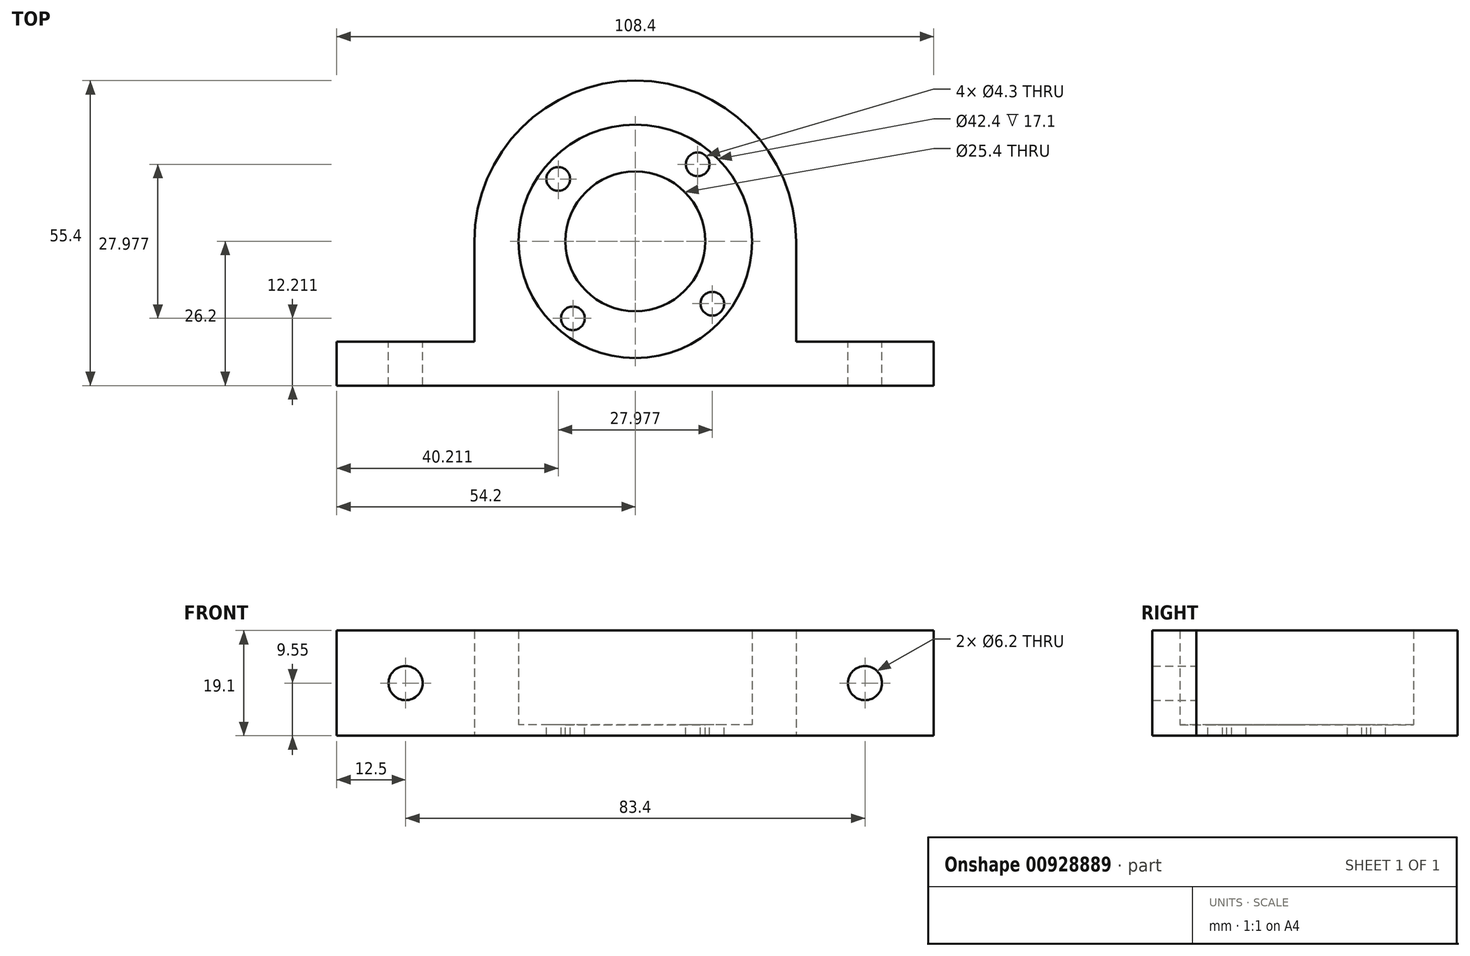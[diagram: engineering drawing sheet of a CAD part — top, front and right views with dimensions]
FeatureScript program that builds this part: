
annotation { "Feature Type Name" : "Feature", "Feature Type Description" : "" }
export const myFeature = defineFeature(function(context is Context, id is Id, definition is map)
    precondition{}
    {
        {
            var Q0;
            Q0=qCreatedBy(makeId("Top.planeOp"),FACE);
            var sketch = newSketch(context, id + "F0", { "sketchPlane" : qUnion([Q0])});
            skCircle(sketch, "E0", {"center": v(0, 0) * mm, "radius": 21.2 * mm});
            skCircle(sketch, "E1", {"center": v(0, 0) * mm, "radius": 26.2 * mm, "construction": true});
            skLineSegment(sketch, "E2", {"start": v(-64.12, -26.2) * mm, "end": v(71.3, -26.2) * mm, "construction": true});
            skLineSegment(sketch, "E3", {"start": v(54.2, -26.2) * mm, "end": v(-54.2, -26.2) * mm});
            skLineSegment(sketch, "E4", {"start": v(-54.2, -26.2) * mm, "end": v(-54.2, -18.2) * mm});
            skLineSegment(sketch, "E5", {"start": v(-54.2, -18.2) * mm, "end": v(-29.2, -18.2) * mm});
            skLineSegment(sketch, "E6", {"start": v(-29.2, -18.2) * mm, "end": v(-29.2, 0) * mm});
            skLineSegment(sketch, "E7", {"start": v(29.2, 0) * mm, "end": v(29.2, -18.2) * mm});
            skLineSegment(sketch, "E8", {"start": v(29.2, -18.2) * mm, "end": v(54.2, -18.2) * mm});
            skLineSegment(sketch, "E9", {"start": v(54.2, -18.2) * mm, "end": v(54.2, -26.2) * mm});
            skArc(sketch, "E10", {"start": v(29.2, 0) * mm, "mid": v(0, 29.2) * mm, "end": v(-29.2, 0) * mm});
            skSolve(sketch);
        }
        {
            var Q0;
            Q0=makeQuery(id+"F0.imprint","IMPRINT",FACE,{"disambiguationData":[TD([[makeQuery(id+"F0.imprint","IMPRINT",EDGE,{"derivedFrom":sQuery(id+"F0.wireOp",EDGE,"E0")}),-1.0]])]});
            extrude(context, id + "F1", {"entities" : qUnion([Q0]), "depth" : 17.1 * mm, "offsetDistance" : 25 * mm});
        }
        {
            var Q0;
            Q0=makeQuery(id+"F1.opExtrude","CAP_FACE",FACE,{"disambiguationData":[OSD([sQuery(id+"F0.wireOp",EDGE,"E0"),sQuery(id+"F0.wireOp",EDGE,"E3"),sQuery(id+"F0.wireOp",EDGE,"E4"),sQuery(id+"F0.wireOp",EDGE,"E5"),sQuery(id+"F0.wireOp",EDGE,"E6"),sQuery(id+"F0.wireOp",EDGE,"E7"),sQuery(id+"F0.wireOp",EDGE,"E8"),sQuery(id+"F0.wireOp",EDGE,"E9"),sQuery(id+"F0.wireOp",EDGE,"E10")])],"isStart":true});
            var sketch = newSketch(context, id + "F2", { "sketchPlane" : qUnion([Q0])});
            skCircle(sketch, "E11", {"center": v(0, 0) * mm, "radius": 12.7 * mm});
            skArc(sketch, "E12", {"start": v(-29.2, 0) * mm, "mid": v(0, -29.2) * mm, "end": v(29.2, 0) * mm});
            skLineSegment(sketch, "E13", {"start": v(-29.2, 0) * mm, "end": v(-29.2, 18.2) * mm});
            skLineSegment(sketch, "E14", {"start": v(29.2, 0) * mm, "end": v(29.2, 18.2) * mm});
            skLineSegment(sketch, "E15", {"start": v(54.2, 26.2) * mm, "end": v(-54.2, 26.2) * mm});
            skLineSegment(sketch, "E16", {"start": v(-54.2, 26.2) * mm, "end": v(-54.2, 18.2) * mm});
            skLineSegment(sketch, "E17", {"start": v(-54.2, 18.2) * mm, "end": v(-29.2, 18.2) * mm});
            skLineSegment(sketch, "E18", {"start": v(54.2, 26.2) * mm, "end": v(54.2, 18.2) * mm});
            skLineSegment(sketch, "E19", {"start": v(54.2, 18.2) * mm, "end": v(29.2, 18.2) * mm});
            skSolve(sketch);
        }
        {
            var Q0;
            Q0=qSketchRegion(id+"F2",true);
            extrude(context, id + "F3", {"entities" : qUnion([Q0]), "operationType" : NewBodyOperationType.ADD, "depth" : 2 * mm, "offsetDistance" : 25 * mm});
        }
        {
            var Q0;
            Q0=makeQuery(id+"F3.opExtrude","CAP_FACE",FACE,{"disambiguationData":[OSD([sQuery(id+"F2.wireOp",EDGE,"E11"),sQuery(id+"F2.wireOp",EDGE,"E12"),sQuery(id+"F2.wireOp",EDGE,"E13"),sQuery(id+"F2.wireOp",EDGE,"E14"),sQuery(id+"F2.wireOp",EDGE,"E15")])],"isStart":true});
            var sketch = newSketch(context, id + "F4", { "sketchPlane" : qUnion([Q0])});
            skCircle(sketch, "E20", {"center": v(0, 0) * mm, "radius": 12.7 * mm});
            skCircle(sketch, "E21", {"center": v(0, 0) * mm, "radius": 21.2 * mm});
            skSolve(sketch);
        }
        {
            var Q0;
            Q0=makeQuery(id+"F4.imprint","IMPRINT",FACE,{"disambiguationData":[TD([[makeQuery(id+"F4.imprint","IMPRINT",EDGE,{"derivedFrom":sQuery(id+"F4.wireOp",EDGE,"E20")}),1.0]])]});
            var sketch = newSketch(context, id + "F5", { "sketchPlane" : qUnion([Q0])});
            skCircle(sketch, "E22", {"center": v(0, 0) * mm, "radius": 18 * mm, "construction": true});
            skLineSegment(sketch, "E23.bottom", {"start": v(-13.99, 11.33) * mm, "end": v(-11.33, -13.99) * mm, "construction": true});
            skLineSegment(sketch, "E23.top", {"start": v(11.33, 13.99) * mm, "end": v(13.99, -11.33) * mm, "construction": true});
            skLineSegment(sketch, "E23.left", {"start": v(-13.99, 11.33) * mm, "end": v(11.33, 13.99) * mm, "construction": true});
            skLineSegment(sketch, "E23.right", {"start": v(-11.33, -13.99) * mm, "end": v(13.99, -11.33) * mm, "construction": true});
            skCircle(sketch, "E24", {"center": v(11.33, 13.99) * mm, "radius": 2.15 * mm});
            skCircle(sketch, "E25.1.0", {"center": v(-13.99, 11.33) * mm, "radius": 2.15 * mm});
            skCircle(sketch, "E25.2.0", {"center": v(-11.33, -13.99) * mm, "radius": 2.15 * mm});
            skCircle(sketch, "E25.3.0", {"center": v(13.99, -11.33) * mm, "radius": 2.15 * mm});
            skLineSegment(sketch, "E26", {"start": v(12.66, 1.33) * mm, "end": v(0, 0) * mm, "construction": true});
            skSolve(sketch);
        }
        {
            var Q0;
            Q0=makeQuery(id+"F5.imprint","IMPRINT",FACE,{"disambiguationData":[TD([[makeQuery(id+"F5.imprint","IMPRINT",EDGE,{"derivedFrom":sQuery(id+"F5.wireOp",EDGE,"E24")}),1.0]])]});
            var Q1;
            Q1=makeQuery(id+"F5.imprint","IMPRINT",FACE,{"disambiguationData":[TD([[makeQuery(id+"F5.imprint","IMPRINT",EDGE,{"derivedFrom":sQuery(id+"F5.wireOp",EDGE,"E25.3.0")}),1.0]])]});
            var Q2;
            Q2=makeQuery(id+"F5.imprint","IMPRINT",FACE,{"disambiguationData":[TD([[makeQuery(id+"F5.imprint","IMPRINT",EDGE,{"derivedFrom":sQuery(id+"F5.wireOp",EDGE,"E25.2.0")}),1.0]])]});
            var Q3;
            Q3=makeQuery(id+"F5.imprint","IMPRINT",FACE,{"disambiguationData":[TD([[makeQuery(id+"F5.imprint","IMPRINT",EDGE,{"derivedFrom":sQuery(id+"F5.wireOp",EDGE,"E25.1.0")}),1.0]])]});
            extrude(context, id + "F6", {"entities" : qUnion([Q0, Q1, Q2, Q3]), "operationType" : NewBodyOperationType.REMOVE, "oppositeDirection" : true, "depth" : 25 * mm, "offsetDistance" : 25 * mm});
        }
        {
            var Q0;
            Q0=makeQuery(id+"F1.opExtrude","SWEPT_FACE",FACE,{"disambiguationData":[OSD([sQuery(id+"F0.wireOp",EDGE,"E5")])]});
            var sketch = newSketch(context, id + "F7", { "sketchPlane" : qUnion([Q0])});
            skLineSegment(sketch, "E27", {"start": v(41.7, -2) * mm, "end": v(41.7, 17.1) * mm, "construction": true});
            skLineSegment(sketch, "E28", {"start": v(-41.7, -2) * mm, "end": v(-41.7, 17.1) * mm, "construction": true});
            skCircle(sketch, "E29", {"center": v(41.7, 7.55) * mm, "radius": 3.1 * mm});
            skCircle(sketch, "E30", {"center": v(-41.7, 7.55) * mm, "radius": 3.1 * mm});
            skSolve(sketch);
        }
        {
            var Q0;
            Q0=qSketchRegion(id+"F7",true);
            extrude(context, id + "F8", {"entities" : qUnion([Q0]), "operationType" : NewBodyOperationType.REMOVE, "endBound" : BoundingType.THROUGH_ALL, "oppositeDirection" : true, "depth" : 25 * mm, "offsetDistance" : 25 * mm});
        }
    });
